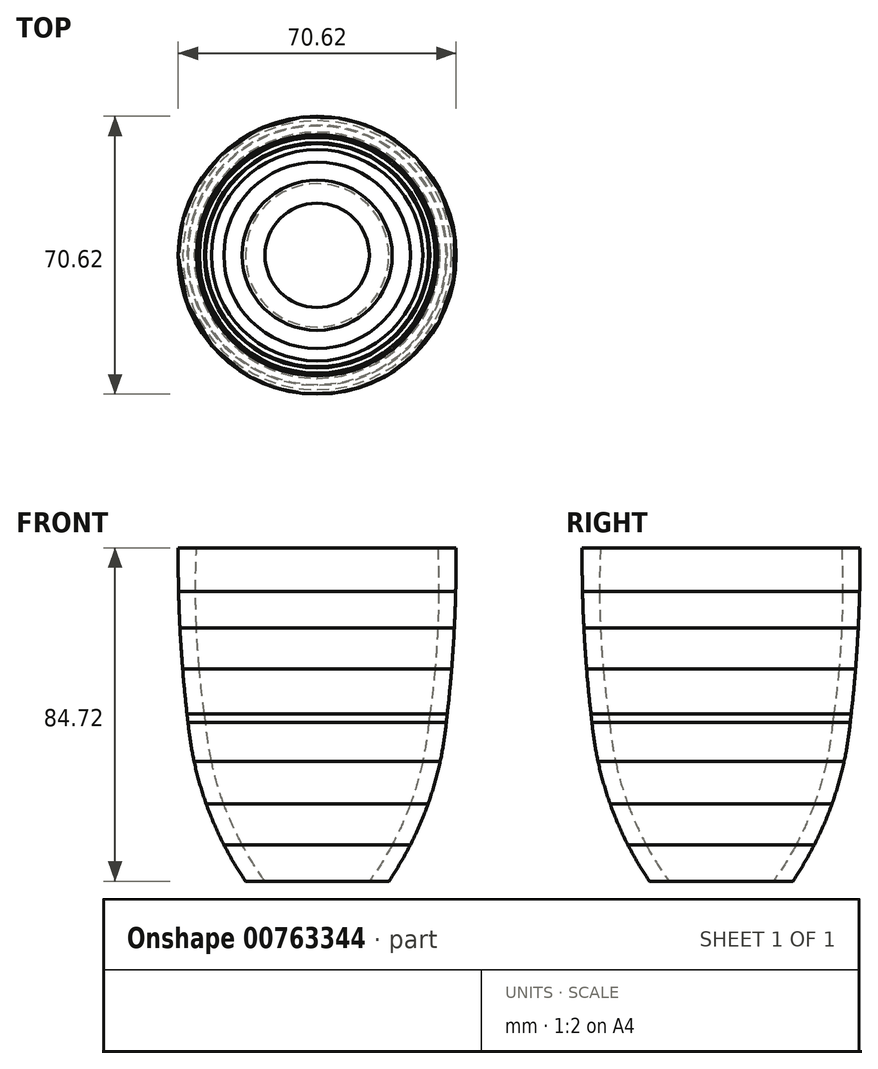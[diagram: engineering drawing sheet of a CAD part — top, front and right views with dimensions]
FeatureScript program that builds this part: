
annotation { "Feature Type Name" : "Feature", "Feature Type Description" : "" }
export const myFeature = defineFeature(function(context is Context, id is Id, definition is map)
    precondition{}
    {
        {
            var Q0;
            Q0=qCreatedBy(makeId("Front.planeOp"),FACE);
            var sketch = newSketch(context, id + "F0", { "sketchPlane" : qUnion([Q0])});
            skArc(sketch, "E0", {"start": v(18.2, -36.53) * mm, "mid": v(28.04, -17.26) * mm, "end": v(32.81, 3.84) * mm});
            skArc(sketch, "E1", {"start": v(32.81, 3.84) * mm, "mid": v(34.75, 25.97) * mm, "end": v(35.3, 48.19) * mm});
            skLineSegment(sketch, "E2", {"start": v(18.2, -36.53) * mm, "end": v(13.25, -36.53) * mm});
            skLineSegment(sketch, "E3", {"start": v(35.3, 48.19) * mm, "end": v(30.63, 48.19) * mm});
            skArc(sketch, "E4", {"start": v(28.32, 3.95) * mm, "mid": v(30.55, 26.01) * mm, "end": v(30.63, 48.19) * mm});
            skArc(sketch, "E5", {"start": v(13.25, -36.53) * mm, "mid": v(23.55, -17.32) * mm, "end": v(28.32, 3.95) * mm});
            skLineSegment(sketch, "E6", {"start": v(19.06, -27.26) * mm, "end": v(23.7, -27.26) * mm});
            skLineSegment(sketch, "E7", {"start": v(23.7, -16.92) * mm, "end": v(28.16, -16.92) * mm});
            skLineSegment(sketch, "E8", {"start": v(26.83, -6.05) * mm, "end": v(31.27, -6.05) * mm});
            skLineSegment(sketch, "E9", {"start": v(29.94, 17.41) * mm, "end": v(34.17, 17.41) * mm});
            skLineSegment(sketch, "E10", {"start": v(30.64, 27.86) * mm, "end": v(34.85, 27.86) * mm});
            skLineSegment(sketch, "E11", {"start": v(30.86, 37.04) * mm, "end": v(35.2, 37.04) * mm});
            skLineSegment(sketch, "E12", {"start": v(0, -36.53) * mm, "end": v(0, 48.41) * mm});
            skLineSegment(sketch, "E13", {"start": v(33.06, 5.98) * mm, "end": v(28.62, 5.98) * mm});
            skSolve(sketch);
        }
        {
            var Q0;
            {var subQ0=sQuery(id+"F0.wireOp",EDGE,"E2");Q0=makeQuery(id+"F0.imprint","IMPRINT",FACE,{"disambiguationData":[TD([[makeQuery(id+"F0.imprint","IMPRINT",EDGE,{"derivedFrom":subQ0}),-1.0]])]});}
            var Q1;
            Q1=sQuery(id+"F0.wireOp",EDGE,"E12");
            revolve(context, id + "F1", {"surfaceOperationType" : NewSurfaceOperationType.NEW, "entities" : qUnion([Q0]), "axis" : qUnion([Q1]), "revolveType" : RevolveType.FULL});
        }
        {
            var Q0;
            {var subQ0=sQuery(id+"F0.wireOp",EDGE,"E6");Q0=makeQuery(id+"F0.imprint","IMPRINT",FACE,{"disambiguationData":[TD([[makeQuery(id+"F0.imprint","IMPRINT",EDGE,{"derivedFrom":subQ0}),1.0]])]});}
            var Q1;
            Q1=sQuery(id+"F0.wireOp",EDGE,"E12");
            revolve(context, id + "F2", {"surfaceOperationType" : NewSurfaceOperationType.NEW, "entities" : qUnion([Q0]), "axis" : qUnion([Q1]), "revolveType" : RevolveType.FULL});
        }
        {
            var Q0;
            {var subQ0=sQuery(id+"F0.wireOp",EDGE,"E7");Q0=makeQuery(id+"F0.imprint","IMPRINT",FACE,{"disambiguationData":[TD([[makeQuery(id+"F0.imprint","IMPRINT",EDGE,{"derivedFrom":subQ0}),1.0]])]});}
            var Q1;
            Q1=sQuery(id+"F0.wireOp",EDGE,"E12");
            revolve(context, id + "F3", {"surfaceOperationType" : NewSurfaceOperationType.NEW, "entities" : qUnion([Q0]), "axis" : qUnion([Q1]), "revolveType" : RevolveType.FULL});
        }
        {
            var Q0;
            {var subQ4=sQuery(id+"F0.wireOp",EDGE,"E8");Q0=makeQuery(id+"F0.imprint","IMPRINT",FACE,{"disambiguationData":[TD([[makeQuery(id+"F0.imprint","IMPRINT",EDGE,{"derivedFrom":subQ4}),1.0]])]});}
            var Q1;
            Q1=sQuery(id+"F0.wireOp",EDGE,"E12");
            revolve(context, id + "F4", {"surfaceOperationType" : NewSurfaceOperationType.NEW, "entities" : qUnion([Q0]), "axis" : qUnion([Q1]), "revolveType" : RevolveType.FULL});
        }
        {
            var Q0;
            {var subQ0=sQuery(id+"F0.wireOp",EDGE,"E9");Q0=makeQuery(id+"F0.imprint","IMPRINT",FACE,{"disambiguationData":[TD([[makeQuery(id+"F0.imprint","IMPRINT",EDGE,{"derivedFrom":subQ0}),-1.0]])]});}
            var Q1;
            Q1=sQuery(id+"F0.wireOp",EDGE,"E12");
            revolve(context, id + "F5", {"surfaceOperationType" : NewSurfaceOperationType.NEW, "entities" : qUnion([Q0]), "axis" : qUnion([Q1]), "revolveType" : RevolveType.FULL});
        }
        {
            var Q0;
            {var subQ0=sQuery(id+"F0.wireOp",EDGE,"E9");Q0=makeQuery(id+"F0.imprint","IMPRINT",FACE,{"disambiguationData":[TD([[makeQuery(id+"F0.imprint","IMPRINT",EDGE,{"derivedFrom":subQ0}),1.0]])]});}
            var Q1;
            Q1=sQuery(id+"F0.wireOp",EDGE,"E12");
            revolve(context, id + "F6", {"surfaceOperationType" : NewSurfaceOperationType.NEW, "entities" : qUnion([Q0]), "axis" : qUnion([Q1]), "revolveType" : RevolveType.FULL});
        }
        {
            var Q0;
            {var subQ0=sQuery(id+"F0.wireOp",EDGE,"E10");Q0=makeQuery(id+"F0.imprint","IMPRINT",FACE,{"disambiguationData":[TD([[makeQuery(id+"F0.imprint","IMPRINT",EDGE,{"derivedFrom":subQ0}),1.0]])]});}
            var Q1;
            Q1=sQuery(id+"F0.wireOp",EDGE,"E12");
            revolve(context, id + "F7", {"surfaceOperationType" : NewSurfaceOperationType.NEW, "entities" : qUnion([Q0]), "axis" : qUnion([Q1]), "revolveType" : RevolveType.FULL});
        }
        {
            var Q0;
            {var subQ0=sQuery(id+"F0.wireOp",EDGE,"E3");Q0=makeQuery(id+"F0.imprint","IMPRINT",FACE,{"disambiguationData":[TD([[makeQuery(id+"F0.imprint","IMPRINT",EDGE,{"derivedFrom":subQ0}),1.0]])]});}
            var Q1;
            Q1=sQuery(id+"F0.wireOp",EDGE,"E12");
            revolve(context, id + "F8", {"surfaceOperationType" : NewSurfaceOperationType.NEW, "entities" : qUnion([Q0]), "axis" : qUnion([Q1]), "revolveType" : RevolveType.FULL});
        }
    });
